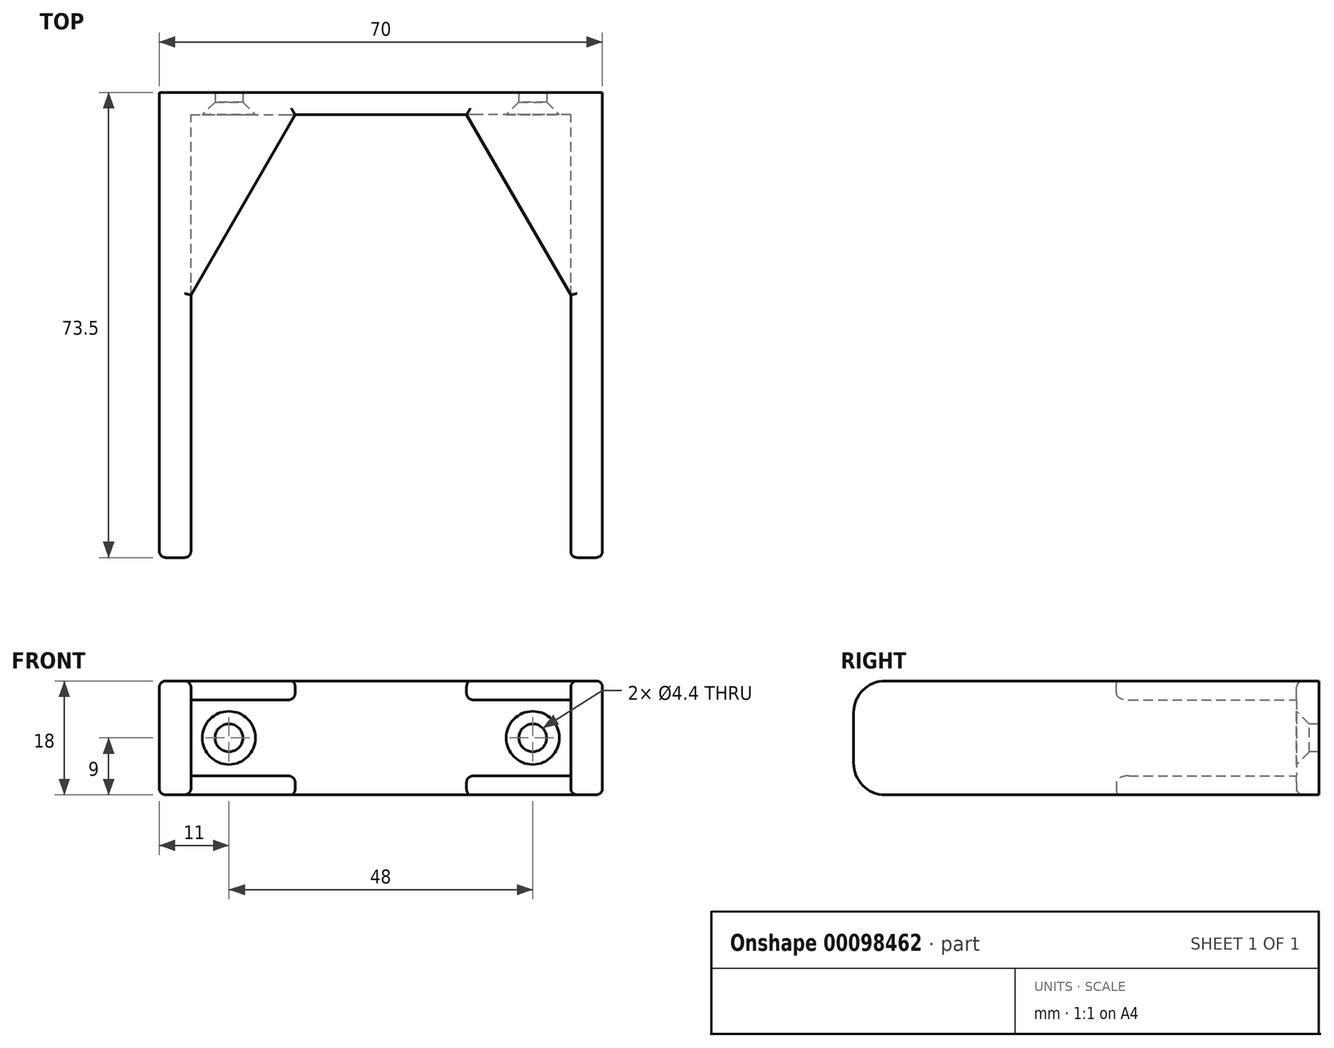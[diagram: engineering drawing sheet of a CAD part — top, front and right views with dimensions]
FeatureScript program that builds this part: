
annotation { "Feature Type Name" : "Feature", "Feature Type Description" : "" }
export const myFeature = defineFeature(function(context is Context, id is Id, definition is map)
    precondition{}
    {
        {
            var Q0;
            Q0=qCreatedBy(makeId("Front.planeOp"),FACE);
            var sketch = newSketch(context, id + "F0", { "sketchPlane" : qUnion([Q0])});
            skLineSegment(sketch, "E0.bottom", {"start": v(35, 9) * mm, "end": v(-35, 9) * mm});
            skLineSegment(sketch, "E0.top", {"start": v(35, -9) * mm, "end": v(-35, -9) * mm});
            skLineSegment(sketch, "E0.left", {"start": v(35, 9) * mm, "end": v(35, -9) * mm});
            skLineSegment(sketch, "E0.right", {"start": v(-35, 9) * mm, "end": v(-35, -9) * mm});
            skPoint(sketch, "E0.middle", {"position": v(0, 0) * mm});
            skCircle(sketch, "E1", {"center": v(24, 0) * mm, "radius": 2.15 * mm, "construction": true});
            skCircle(sketch, "E2.MirrorC", {"center": v(-24, 0) * mm, "radius": 2.15 * mm, "construction": true});
            skCircle(sketch, "E3", {"center": v(-24, 0) * mm, "radius": 3.85 * mm, "construction": true});
            skSolve(sketch);
        }
        {
            var Q0;
            Q0=qSketchRegion(id+"F0",true);
            extrude(context, id + "F1", {"entities" : qUnion([Q0]), "depth" : 3.5 * mm});
        }
        {
            var Q0;
            Q0=makeQuery(id+"F1.opExtrude","CAP_FACE",FACE,{"disambiguationData":[OSD([sQuery(id+"F0.wireOp",EDGE,"E0.bottom"),sQuery(id+"F0.wireOp",EDGE,"E0.top"),sQuery(id+"F0.wireOp",EDGE,"E0.left"),sQuery(id+"F0.wireOp",EDGE,"E0.right")])],"isStart":false});
            var sketch = newSketch(context, id + "F2", { "sketchPlane" : qUnion([Q0])});
            skLineSegment(sketch, "E4.bottom", {"start": v(35, 9) * mm, "end": v(30, 9) * mm});
            skLineSegment(sketch, "E4.top", {"start": v(35, -9) * mm, "end": v(30, -9) * mm});
            skLineSegment(sketch, "E4.left", {"start": v(35, 9) * mm, "end": v(35, -9) * mm});
            skLineSegment(sketch, "E4.right", {"start": v(30, 9) * mm, "end": v(30, -9) * mm});
            skSolve(sketch);
        }
        {
            var Q0;
            Q0=qSketchRegion(id+"F2",true);
            extrude(context, id + "F3", {"entities" : qUnion([Q0]), "depth" : 70 * mm});
        }
        {
            var Q0;
            Q0=makeQuery(id+"F3.opExtrude","SWEPT_FACE",FACE,{"disambiguationData":[OSD([sQuery(id+"F2.wireOp",EDGE,"E4.top")])]});
            var sketch = newSketch(context, id + "F4", { "sketchPlane" : qUnion([Q0])});
            skLineSegment(sketch, "E5.0", {"start": v(30, 3.5) * mm, "end": v(13.54, 3.5) * mm});
            skLineSegment(sketch, "E6", {"start": v(13.54, 3.5) * mm, "end": v(30, 32) * mm});
            skPoint(sketch, "E7.orphan", {"position": v(-35, 3.5) * mm});
            skLineSegment(sketch, "E8", {"start": v(30, 32) * mm, "end": v(30, 3.5) * mm});
            skPoint(sketch, "E9.orphan", {"position": v(35, 3.5) * mm});
            skSolve(sketch);
        }
        {
            var Q0;
            Q0=qSketchRegion(id+"F4",true);
            extrude(context, id + "F5", {"entities" : qUnion([Q0]), "oppositeDirection" : true, "depth" : 3 * mm});
        }
        {
            var Q0;
            Q0=makeQuery(id+"F5.opExtrude","SWEPT_BODY",BODY,{"disambiguationData":[OSD([sQuery(id+"F4.wireOp",EDGE,"E5.0"),sQuery(id+"F4.wireOp",EDGE,"E6"),sQuery(id+"F4.wireOp",EDGE,"E8")])]});
            var Q1;
            Q1=qCreatedBy(makeId("Top.planeOp"),FACE);
            mirror(context, id + "F6", {"entities" : qUnion([Q0]), "mirrorPlane" : qUnion([Q1])});
        }
        {
            var Q0;
            Q0=makeQuery(id+"F3.opExtrude","SWEPT_BODY",BODY,{"disambiguationData":[OSD([sQuery(id+"F2.wireOp",EDGE,"E4.bottom"),sQuery(id+"F2.wireOp",EDGE,"E4.top"),sQuery(id+"F2.wireOp",EDGE,"E4.left"),sQuery(id+"F2.wireOp",EDGE,"E4.right")])]});
            var Q1;
            Q1=makeQuery(id+"F5.opExtrude","SWEPT_BODY",BODY,{"disambiguationData":[OSD([sQuery(id+"F4.wireOp",EDGE,"E5.0"),sQuery(id+"F4.wireOp",EDGE,"E6"),sQuery(id+"F4.wireOp",EDGE,"E8")])]});
            var Q2;
            Q2=makeQuery(id+"F6.opPattern","COPY",BODY,{"derivedFrom":makeQuery(id+"F5.opExtrude","SWEPT_BODY",BODY,{"disambiguationData":[OSD([sQuery(id+"F4.wireOp",EDGE,"E5.0"),sQuery(id+"F4.wireOp",EDGE,"E6"),sQuery(id+"F4.wireOp",EDGE,"E8")])]}),"instanceName":"1"});
            var Q3;
            Q3=qCreatedBy(makeId("Right.planeOp"),FACE);
            mirror(context, id + "F7", {"operationType" : NewBodyOperationType.ADD, "entities" : qUnion([Q0, Q1, Q2]), "mirrorPlane" : qUnion([Q3])});
        }
        {
            var Q0;
            Q0=makeQuery(id+"F7.opPattern","COPY",EDGE,{"derivedFrom":makeQuery(id+"F3.opExtrude","CAP_EDGE",EDGE,{"disambiguationData":[OSD([sQuery(id+"F2.wireOp",EDGE,"E4.top")])],"isStart":false}),"instanceName":"1"});
            var Q1;
            Q1=makeQuery(id+"F7.opPattern","COPY",EDGE,{"derivedFrom":makeQuery(id+"F3.opExtrude","CAP_EDGE",EDGE,{"disambiguationData":[OSD([sQuery(id+"F2.wireOp",EDGE,"E4.bottom")])],"isStart":false}),"instanceName":"1"});
            var Q2;
            Q2=makeQuery(id+"F3.opExtrude","CAP_EDGE",EDGE,{"disambiguationData":[OSD([sQuery(id+"F2.wireOp",EDGE,"E4.top")])],"isStart":false});
            var Q3;
            Q3=makeQuery(id+"F3.opExtrude","CAP_EDGE",EDGE,{"disambiguationData":[OSD([sQuery(id+"F2.wireOp",EDGE,"E4.bottom")])],"isStart":false});
            fillet(context, id + "F8", {"entities" : qUnion([Q0, Q1, Q2, Q3]), "radius" : 5 * mm, "tangentPropagation" : true, "allowEdgeOverflow" : false});
        }
        {
            var Q0;
            Q0=makeQuery(id+"F7.boolean.opBoolean","MERGE",EDGE,{"derivedFrom":[makeQuery(id+"F1.opExtrude","SWEPT_EDGE",EDGE,{"disambiguationData":[OSD([sQuery(id+"F0.wireOp",EDGE,"E0.top"),sQuery(id+"F0.wireOp",EDGE,"E0.right")])]}),makeQuery(id+"F7.opPattern","COPY",EDGE,{"derivedFrom":makeQuery(id+"F3.opExtrude","SWEPT_EDGE",EDGE,{"disambiguationData":[OSD([sQuery(id+"F2.wireOp",EDGE,"E4.top"),sQuery(id+"F2.wireOp",EDGE,"E4.left")])]}),"instanceName":"1"})]});
            var Q1;
            Q1=makeQuery(id+"F7.boolean.opBoolean","MERGE",EDGE,{"derivedFrom":[makeQuery(id+"F1.opExtrude","SWEPT_EDGE",EDGE,{"disambiguationData":[OSD([sQuery(id+"F0.wireOp",EDGE,"E0.top"),sQuery(id+"F0.wireOp",EDGE,"E0.left")])]}),makeQuery(id+"F3.opExtrude","SWEPT_EDGE",EDGE,{"disambiguationData":[OSD([sQuery(id+"F2.wireOp",EDGE,"E4.top"),sQuery(id+"F2.wireOp",EDGE,"E4.left")])]})]});
            var Q2;
            Q2=makeQuery(id+"F7.opPattern","COPY",EDGE,{"derivedFrom":makeQuery(id+"F3.opExtrude","SWEPT_EDGE",EDGE,{"disambiguationData":[OSD([sQuery(id+"F0.wireOp",EDGE,"E0.top"),sQuery(id+"F2.wireOp",EDGE,"E4.top"),sQuery(id+"F2.wireOp",EDGE,"E4.right")])]}),"instanceName":"1"});
            var Q3;
            Q3=makeQuery(id+"F3.opExtrude","SWEPT_EDGE",EDGE,{"disambiguationData":[OSD([sQuery(id+"F0.wireOp",EDGE,"E0.top"),sQuery(id+"F2.wireOp",EDGE,"E4.top"),sQuery(id+"F2.wireOp",EDGE,"E4.right")])]});
            var Q4;
            Q4=makeQuery(id+"F7.opPattern","COPY",EDGE,{"derivedFrom":makeQuery(id+"F5.opExtrude","CAP_EDGE",EDGE,{"disambiguationData":[OSD([sQuery(id+"F4.wireOp",EDGE,"E6")])],"isStart":true}),"instanceName":"1"});
            var Q5;
            Q5=makeQuery(id+"F1.opExtrude","CAP_EDGE",EDGE,{"disambiguationData":[OSD([sQuery(id+"F0.wireOp",EDGE,"E0.top")])],"isStart":false});
            var Q6;
            Q6=makeQuery(id+"F6.opPattern","COPY",EDGE,{"derivedFrom":makeQuery(id+"F5.opExtrude","CAP_EDGE",EDGE,{"disambiguationData":[OSD([sQuery(id+"F4.wireOp",EDGE,"E6")])],"isStart":true}),"instanceName":"1"});
            var Q7;
            Q7=makeQuery(id+"F7.opPattern","COPY",EDGE,{"derivedFrom":makeQuery(id+"F6.opPattern","COPY",EDGE,{"derivedFrom":makeQuery(id+"F5.opExtrude","CAP_EDGE",EDGE,{"disambiguationData":[OSD([sQuery(id+"F4.wireOp",EDGE,"E6")])],"isStart":true}),"instanceName":"1"}),"instanceName":"1"});
            var Q8;
            Q8=makeQuery(id+"F1.opExtrude","CAP_EDGE",EDGE,{"disambiguationData":[OSD([sQuery(id+"F0.wireOp",EDGE,"E0.bottom")])],"isStart":false});
            var Q9;
            Q9=makeQuery(id+"F6.opPattern","COPY",EDGE,{"derivedFrom":makeQuery(id+"F5.opExtrude","CAP_EDGE",EDGE,{"disambiguationData":[OSD([sQuery(id+"F4.wireOp",EDGE,"E6")])],"isStart":false}),"instanceName":"1"});
            var Q10;
            Q10=makeQuery(id+"F5.opExtrude","CAP_EDGE",EDGE,{"disambiguationData":[OSD([sQuery(id+"F4.wireOp",EDGE,"E6")])],"isStart":false});
            var Q11;
            Q11=makeQuery(id+"F7.opPattern","COPY",EDGE,{"derivedFrom":makeQuery(id+"F6.opPattern","COPY",EDGE,{"derivedFrom":makeQuery(id+"F5.opExtrude","CAP_EDGE",EDGE,{"disambiguationData":[OSD([sQuery(id+"F4.wireOp",EDGE,"E6")])],"isStart":false}),"instanceName":"1"}),"instanceName":"1"});
            var Q12;
            Q12=makeQuery(id+"F7.opPattern","COPY",EDGE,{"derivedFrom":makeQuery(id+"F5.opExtrude","CAP_EDGE",EDGE,{"disambiguationData":[OSD([sQuery(id+"F4.wireOp",EDGE,"E6")])],"isStart":false}),"instanceName":"1"});
            var Q13;
            Q13=makeQuery(id+"F5.opExtrude","CAP_EDGE",EDGE,{"disambiguationData":[OSD([sQuery(id+"F4.wireOp",EDGE,"E6")])],"isStart":true});
            fillet(context, id + "F9", {"entities" : qUnion([Q0, Q1, Q2, Q3, Q4, Q5, Q6, Q7, Q8, Q9, Q10, Q11, Q12, Q13]), "radius" : 1 * mm, "tangentPropagation" : true, "allowEdgeOverflow" : false});
        }
        {
            var Q0;
            {var subQ0=sQuery(id+"F2.wireOp",EDGE,"E4.right");Q0=makeQuery(id+"F2.imprint","IMPRINT",FACE,{"disambiguationData":[TD([[makeQuery(id+"F2.imprint","IMPRINT",EDGE,{"derivedFrom":subQ0}),-1.0]])]});}
            var sketch = newSketch(context, id + "F10", { "sketchPlane" : qUnion([Q0])});
            skCircle(sketch, "E10.0", {"center": v(-24, 0) * mm, "radius": 2.15 * mm, "construction": true});
            skCircle(sketch, "E10.1", {"center": v(24, 0) * mm, "radius": 2.15 * mm, "construction": true});
            skSolve(sketch);
        }
        {
            var Q0;
            Q0=sQuery(id+"F10.wireOp",VERTEX,"E10.0.center");
            var Q1;
            Q1=sQuery(id+"F10.wireOp",VERTEX,"E10.1.center");
            var Q2;
            Q2=makeQuery(id+"F1.opExtrude","SWEPT_BODY",BODY,{"disambiguationData":[OSD([sQuery(id+"F0.wireOp",EDGE,"E0.bottom"),sQuery(id+"F0.wireOp",EDGE,"E0.top"),sQuery(id+"F0.wireOp",EDGE,"E0.left"),sQuery(id+"F0.wireOp",EDGE,"E0.right")])]});
            hole(context, id + "F11", {"style" : HoleStyle.C_SINK, "endStyle" : HoleEndStyle.THROUGH, "holeDiameter" : 4.4 * mm, "cSinkDiameter" : 8.4 * mm, "cSinkAngle" : 90 * degree, "locations" : qUnion([Q0, Q1]), "scope" : qUnion([Q2]), "isTappedThrough" : true});
        }
    });
